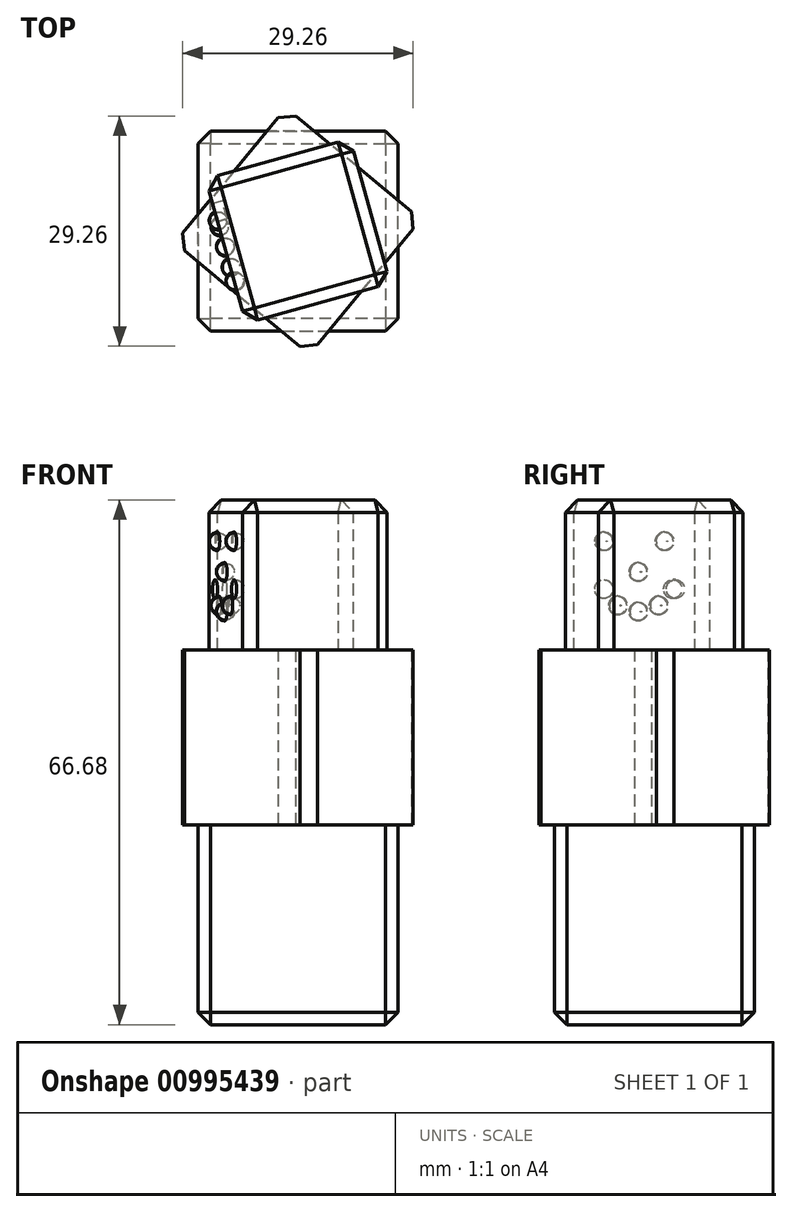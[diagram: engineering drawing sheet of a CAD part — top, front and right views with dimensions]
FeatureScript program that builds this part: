
annotation { "Feature Type Name" : "Feature", "Feature Type Description" : "" }
export const myFeature = defineFeature(function(context is Context, id is Id, definition is map)
    precondition{}
    {
        {
            var Q0;
            Q0=qCreatedBy(makeId("Top.planeOp"),FACE);
            var sketch = newSketch(context, id + "F0", { "sketchPlane" : qUnion([Q0])});
            skLineSegment(sketch, "E0.bottom", {"start": v(0, 0) * mm, "end": v(25.4, 0) * mm});
            skLineSegment(sketch, "E0.top", {"start": v(0, 25.4) * mm, "end": v(25.4, 25.4) * mm});
            skLineSegment(sketch, "E0.left", {"start": v(0, 0) * mm, "end": v(0, 25.4) * mm});
            skLineSegment(sketch, "E0.right", {"start": v(25.4, 0) * mm, "end": v(25.4, 25.4) * mm});
            skSolve(sketch);
        }
        {
            var Q0;
            Q0=makeQuery(id+"F0.imprint","IMPRINT",FACE,{"disambiguationData":[TD([[makeQuery(id+"F0.imprint","IMPRINT",EDGE,{"derivedFrom":sQuery(id+"F0.wireOp",EDGE,"E0.bottom")}),1.0]])]});
            extrude(context, id + "F1", {"entities" : qUnion([Q0]), "depth" : 25.4 * mm, "offsetDistance" : 25.4 * mm});
        }
        {
            var Q0;
            Q0=makeQuery(id+"F1.opExtrude","CAP_FACE",FACE,{"disambiguationData":[OSD([sQuery(id+"F0.wireOp",EDGE,"E0.bottom"),sQuery(id+"F0.wireOp",EDGE,"E0.top"),sQuery(id+"F0.wireOp",EDGE,"E0.left"),sQuery(id+"F0.wireOp",EDGE,"E0.right")])],"isStart":false});
            var sketch = newSketch(context, id + "F2", { "sketchPlane" : qUnion([Q0])});
            skPoint(sketch, "E1", {"position": v(12.7, 12.7) * mm});
            skLineSegment(sketch, "E2", {"start": v(-2.94, 11.2) * mm, "end": v(14.2, -2.94) * mm});
            skLineSegment(sketch, "E3", {"start": v(14.2, -2.94) * mm, "end": v(28.34, 14.2) * mm});
            skLineSegment(sketch, "E4", {"start": v(28.34, 14.2) * mm, "end": v(11.2, 28.34) * mm});
            skLineSegment(sketch, "E5", {"start": v(11.2, 28.34) * mm, "end": v(-2.94, 11.2) * mm});
            skSolve(sketch);
        }
        {
            var Q0;
            Q0 = qSketchRegion(id + "F2", true);
            extrude(context, id + "F3", {"entities" : qUnion([Q0]), "operationType" : NewBodyOperationType.ADD, "depth" : 22.22 * mm, "offsetDistance" : 25.4 * mm});
        }
        {
            var Q0;
            Q0=makeQuery(id+"F3.opExtrude","CAP_FACE",FACE,{"disambiguationData":[OSD([sQuery(id+"F2.wireOp",EDGE,"E2"),sQuery(id+"F2.wireOp",EDGE,"E3"),sQuery(id+"F2.wireOp",EDGE,"E4"),sQuery(id+"F2.wireOp",EDGE,"E5")])],"isStart":false});
            var sketch = newSketch(context, id + "F4", { "sketchPlane" : qUnion([Q0])});
            skLineSegment(sketch, "E6", {"start": v(0.98, 19.34) * mm, "end": v(6.06, 0.98) * mm});
            skLineSegment(sketch, "E7", {"start": v(6.06, 0.98) * mm, "end": v(24.42, 6.06) * mm});
            skLineSegment(sketch, "E8", {"start": v(24.42, 6.06) * mm, "end": v(19.34, 24.42) * mm});
            skLineSegment(sketch, "E9", {"start": v(19.34, 24.42) * mm, "end": v(0.98, 19.34) * mm});
            skPoint(sketch, "E10", {"position": v(12.7, 12.7) * mm});
            skSolve(sketch);
        }
        {
            var Q0;
            Q0 = qSketchRegion(id + "F4", true);
            extrude(context, id + "F5", {"entities" : qUnion([Q0]), "operationType" : NewBodyOperationType.ADD, "depth" : 19.05 * mm, "offsetDistance" : 25.4 * mm});
        }
        {
            var Q0;
            Q0=makeQuery(id+"F5.opExtrude","SWEPT_EDGE",EDGE,{"disambiguationData":[OSD([sQuery(id+"F4.wireOp",EDGE,"E6"),sQuery(id+"F4.wireOp",EDGE,"E9")])]});
            var Q1;
            Q1=makeQuery(id+"F5.opExtrude","SWEPT_EDGE",EDGE,{"disambiguationData":[OSD([sQuery(id+"F4.wireOp",EDGE,"E6"),sQuery(id+"F4.wireOp",EDGE,"E7")])]});
            var Q2;
            Q2=makeQuery(id+"F5.opExtrude","CAP_FACE",FACE,{"disambiguationData":[OSD([sQuery(id+"F4.wireOp",EDGE,"E6"),sQuery(id+"F4.wireOp",EDGE,"E7"),sQuery(id+"F4.wireOp",EDGE,"E8"),sQuery(id+"F4.wireOp",EDGE,"E9")])],"isStart":false});
            var Q3;
            Q3=makeQuery(id+"F5.opExtrude","SWEPT_EDGE",EDGE,{"disambiguationData":[OSD([sQuery(id+"F4.wireOp",EDGE,"E8"),sQuery(id+"F4.wireOp",EDGE,"E9")])]});
            var Q4;
            Q4=makeQuery(id+"F5.opExtrude","SWEPT_EDGE",EDGE,{"disambiguationData":[OSD([sQuery(id+"F4.wireOp",EDGE,"E7"),sQuery(id+"F4.wireOp",EDGE,"E8")])]});
            var Q5;
            Q5=makeQuery(id+"F3.opExtrude","SWEPT_EDGE",EDGE,{"disambiguationData":[OSD([sQuery(id+"F2.wireOp",EDGE,"E3"),sQuery(id+"F2.wireOp",EDGE,"E4")])]});
            var Q6;
            Q6=makeQuery(id+"F3.opExtrude","SWEPT_EDGE",EDGE,{"disambiguationData":[OSD([sQuery(id+"F2.wireOp",EDGE,"E4"),sQuery(id+"F2.wireOp",EDGE,"E5")])]});
            var Q7;
            Q7=makeQuery(id+"F3.opExtrude","SWEPT_EDGE",EDGE,{"disambiguationData":[OSD([sQuery(id+"F2.wireOp",EDGE,"E2"),sQuery(id+"F2.wireOp",EDGE,"E5")])]});
            var Q8;
            Q8=makeQuery(id+"F3.opExtrude","SWEPT_EDGE",EDGE,{"disambiguationData":[OSD([sQuery(id+"F2.wireOp",EDGE,"E2"),sQuery(id+"F2.wireOp",EDGE,"E3")])]});
            var Q9;
            Q9=makeQuery(id+"F1.opExtrude","SWEPT_EDGE",EDGE,{"disambiguationData":[OSD([sQuery(id+"F0.wireOp",EDGE,"E0.bottom"),sQuery(id+"F0.wireOp",EDGE,"E0.left")])]});
            var Q10;
            Q10=makeQuery(id+"F1.opExtrude","SWEPT_EDGE",EDGE,{"disambiguationData":[OSD([sQuery(id+"F0.wireOp",EDGE,"E0.bottom"),sQuery(id+"F0.wireOp",EDGE,"E0.right")])]});
            var Q11;
            Q11=makeQuery(id+"F1.opExtrude","SWEPT_EDGE",EDGE,{"disambiguationData":[OSD([sQuery(id+"F0.wireOp",EDGE,"E0.top"),sQuery(id+"F0.wireOp",EDGE,"E0.right")])]});
            var Q12;
            Q12=makeQuery(id+"F1.opExtrude","SWEPT_EDGE",EDGE,{"disambiguationData":[OSD([sQuery(id+"F0.wireOp",EDGE,"E0.top"),sQuery(id+"F0.wireOp",EDGE,"E0.left")])]});
            var Q13;
            Q13=makeQuery(id+"F1.opExtrude","CAP_FACE",FACE,{"disambiguationData":[OSD([sQuery(id+"F0.wireOp",EDGE,"E0.bottom"),sQuery(id+"F0.wireOp",EDGE,"E0.top"),sQuery(id+"F0.wireOp",EDGE,"E0.left"),sQuery(id+"F0.wireOp",EDGE,"E0.right")])],"isStart":true});
            chamfer(context, id + "F6", {"entities" : qUnion([Q0, Q1, Q2, Q3, Q4, Q5, Q6, Q7, Q8, Q9, Q10, Q11, Q12, Q13]), "width" : 1.59 * mm, "tangentPropagation" : true});
        }
        {
            var Q0;
            Q0=makeQuery(id+"F5.opExtrude","SWEPT_FACE",FACE,{"disambiguationData":[OSD([sQuery(id+"F4.wireOp",EDGE,"E6")])]});
            var sketch = newSketch(context, id + "F7", { "sketchPlane" : qUnion([Q0])});
            skCircle(sketch, "E11", {"center": v(-12.84, 61.4) * mm, "radius": 1.2 * mm});
            skCircle(sketch, "E12", {"center": v(-4.86, 61.4) * mm, "radius": 1.2 * mm});
            skCircle(sketch, "E13", {"center": v(-9.38, 57.51) * mm, "radius": 1.2 * mm});
            skCircle(sketch, "E14", {"center": v(-13.92, 55.33) * mm, "radius": 1.2 * mm});
            skCircle(sketch, "E15", {"center": v(-12.06, 53.25) * mm, "radius": 1.2 * mm});
            skCircle(sketch, "E16", {"center": v(-9.38, 52.48) * mm, "radius": 1.2 * mm});
            skCircle(sketch, "E17", {"center": v(-6.7, 53.25) * mm, "radius": 1.2 * mm});
            skCircle(sketch, "E18", {"center": v(-4.83, 55.33) * mm, "radius": 1.2 * mm});
            skArc(sketch, "E19", {"start": v(-13.92, 55.33) * mm, "mid": v(-9.38, 52.48) * mm, "end": v(-4.83, 55.33) * mm});
            skSolve(sketch);
        }
        {
            var Q0;
            Q0 = qSketchRegion(id + "F7", true);
            extrude(context, id + "F8", {"entities" : qUnion([Q0]), "operationType" : NewBodyOperationType.REMOVE, "oppositeDirection" : true, "depth" : 1.27 * mm, "offsetDistance" : 25.4 * mm});
        }
        {
            var Q0;
            Q0=makeQuery(id+"F8.boolean.opBoolean","COPY",FACE,{"derivedFrom":makeQuery(id+"F8.opExtrude","CAP_FACE",FACE,{"disambiguationData":[OSD([sQuery(id+"F7.wireOp",EDGE,"E11")])],"isStart":false})});
            var Q1;
            Q1=makeQuery(id+"F8.boolean.opBoolean","COPY",FACE,{"derivedFrom":makeQuery(id+"F8.opExtrude","CAP_FACE",FACE,{"disambiguationData":[OSD([sQuery(id+"F7.wireOp",EDGE,"E12")])],"isStart":false})});
            var Q2;
            Q2=makeQuery(id+"F8.boolean.opBoolean","COPY",FACE,{"derivedFrom":makeQuery(id+"F8.opExtrude","CAP_FACE",FACE,{"disambiguationData":[OSD([sQuery(id+"F7.wireOp",EDGE,"E13")])],"isStart":false})});
            var Q3;
            Q3=makeQuery(id+"F8.boolean.opBoolean","COPY",FACE,{"derivedFrom":makeQuery(id+"F8.opExtrude","CAP_FACE",FACE,{"disambiguationData":[OSD([sQuery(id+"F7.wireOp",EDGE,"E14")])],"isStart":false})});
            var Q4;
            Q4=makeQuery(id+"F8.boolean.opBoolean","COPY",FACE,{"derivedFrom":makeQuery(id+"F8.opExtrude","CAP_FACE",FACE,{"disambiguationData":[OSD([sQuery(id+"F7.wireOp",EDGE,"E15")])],"isStart":false})});
            var Q5;
            Q5=makeQuery(id+"F8.boolean.opBoolean","COPY",FACE,{"derivedFrom":makeQuery(id+"F8.opExtrude","CAP_FACE",FACE,{"disambiguationData":[OSD([sQuery(id+"F7.wireOp",EDGE,"E16")])],"isStart":false})});
            var Q6;
            Q6=makeQuery(id+"F8.boolean.opBoolean","COPY",FACE,{"derivedFrom":makeQuery(id+"F8.opExtrude","CAP_FACE",FACE,{"disambiguationData":[OSD([sQuery(id+"F7.wireOp",EDGE,"E17")])],"isStart":false})});
            var Q7;
            Q7=makeQuery(id+"F8.boolean.opBoolean","COPY",FACE,{"derivedFrom":makeQuery(id+"F8.opExtrude","CAP_FACE",FACE,{"disambiguationData":[OSD([sQuery(id+"F7.wireOp",EDGE,"E18")])],"isStart":false})});
            fillet(context, id + "F9", {"entities" : qUnion([Q0, Q1, Q2, Q3, Q4, Q5, Q6, Q7]), "radius" : 1.14 * mm, "tangentPropagation" : true, "allowEdgeOverflow" : false});
        }
    });
